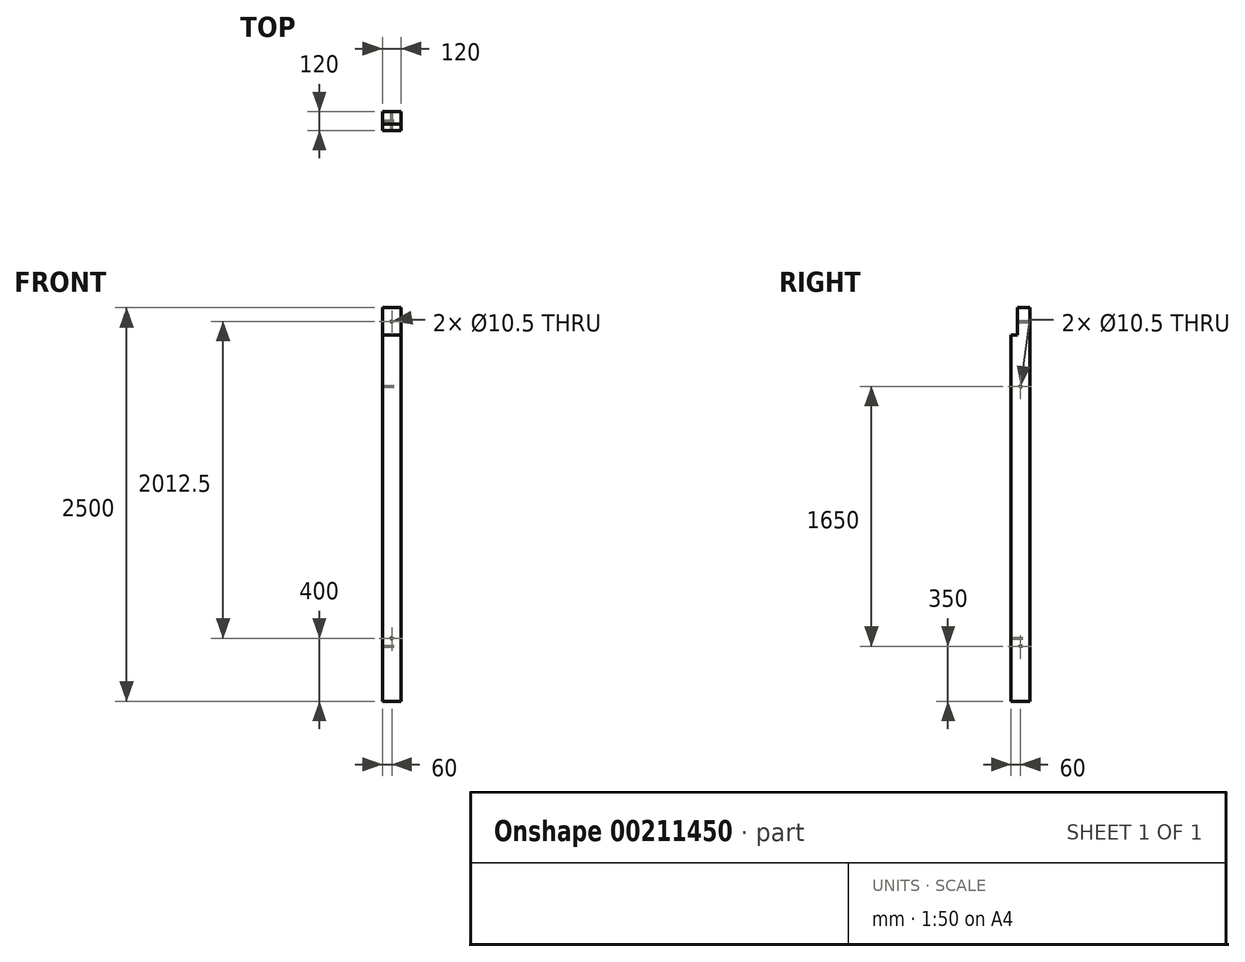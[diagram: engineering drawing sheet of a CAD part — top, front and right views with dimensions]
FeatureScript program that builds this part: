
annotation { "Feature Type Name" : "Feature", "Feature Type Description" : "" }
export const myFeature = defineFeature(function(context is Context, id is Id, definition is map)
    precondition{}
    {
        {
            var Q0;
            Q0=qCreatedBy(makeId("Top.planeOp"),FACE);
            var sketch = newSketch(context, id + "F0", { "sketchPlane" : qUnion([Q0])});
            skLineSegment(sketch, "E0", {"start": v(0, 0) * mm, "end": v(0, 330.83) * mm, "construction": true});
            skLineSegment(sketch, "E1", {"start": v(-296.67, 0) * mm, "end": v(360, 0) * mm, "construction": true});
            skLineSegment(sketch, "E2.bottom", {"start": v(60, 60) * mm, "end": v(-60, 60) * mm});
            skLineSegment(sketch, "E2.top", {"start": v(60, -60) * mm, "end": v(-60, -60) * mm});
            skLineSegment(sketch, "E2.left", {"start": v(60, 60) * mm, "end": v(60, -60) * mm});
            skLineSegment(sketch, "E2.right", {"start": v(-60, 60) * mm, "end": v(-60, -60) * mm});
            skPoint(sketch, "E2.middle", {"position": v(0, 0) * mm});
            skPoint(sketch, "E3.visualSharp", {"position": v(-60, 60) * mm});
            skPoint(sketch, "E4.visualSharp", {"position": v(60, 60) * mm});
            skPoint(sketch, "E5.visualSharp", {"position": v(-60, -60) * mm});
            skPoint(sketch, "E6.visualSharp", {"position": v(60, -60) * mm});
            skSolve(sketch);
        }
        {
            var Q0;
            Q0=qSketchRegion(id+"F0",true);
            extrude(context, id + "F1", {"entities" : qUnion([Q0]), "depth" : 2500 * mm, "symmetric" : true});
        }
        {
            var Q0;
            Q0=makeQuery(id+"F1.opExtrude","SWEPT_FACE",FACE,{"disambiguationData":[OSD([sQuery(id+"F0.wireOp",EDGE,"E2.left")])]});
            var sketch = newSketch(context, id + "F2", { "sketchPlane" : qUnion([Q0])});
            skLineSegment(sketch, "E7.bottom", {"start": v(-60, 1250) * mm, "end": v(-20, 1250) * mm});
            skLineSegment(sketch, "E7.top", {"start": v(-60, 1075) * mm, "end": v(-20, 1075) * mm});
            skLineSegment(sketch, "E7.left", {"start": v(-60, 1250) * mm, "end": v(-60, 1075) * mm});
            skLineSegment(sketch, "E7.right", {"start": v(-20, 1250) * mm, "end": v(-20, 1075) * mm});
            skSolve(sketch);
        }
        {
            var Q0;
            Q0=qSketchRegion(id+"F2",true);
            extrude(context, id + "F3", {"entities" : qUnion([Q0]), "operationType" : NewBodyOperationType.REMOVE, "endBound" : BoundingType.UP_TO_NEXT, "oppositeDirection" : true, "depth" : 25 * mm});
        }
        {
            var Q0;
            Q0=makeQuery(id+"F1.opExtrude","SWEPT_FACE",FACE,{"disambiguationData":[OSD([sQuery(id+"F0.wireOp",EDGE,"E2.bottom")])]});
            var sketch = newSketch(context, id + "F4", { "sketchPlane" : qUnion([Q0])});
            skCircle(sketch, "E8", {"center": v(0, 1162.5) * mm, "radius": 5.25 * mm});
            skCircle(sketch, "E9", {"center": v(0, -850) * mm, "radius": 5.25 * mm});
            skSolve(sketch);
        }
        {
            var Q0;
            Q0=qSketchRegion(id+"F4",true);
            extrude(context, id + "F5", {"entities" : qUnion([Q0]), "operationType" : NewBodyOperationType.REMOVE, "endBound" : BoundingType.THROUGH_ALL, "oppositeDirection" : true, "depth" : 25 * mm});
        }
        {
            var Q0;
            Q0=makeQuery(id+"F1.opExtrude","SWEPT_FACE",FACE,{"disambiguationData":[OSD([sQuery(id+"F0.wireOp",EDGE,"E2.left")])]});
            var sketch = newSketch(context, id + "F6", { "sketchPlane" : qUnion([Q0])});
            skCircle(sketch, "E10", {"center": v(0, -900) * mm, "radius": 5.25 * mm});
            skCircle(sketch, "E11", {"center": v(0, 750) * mm, "radius": 5.25 * mm});
            skSolve(sketch);
        }
        {
            var Q0;
            Q0=qSketchRegion(id+"F6",true);
            extrude(context, id + "F7", {"entities" : qUnion([Q0]), "operationType" : NewBodyOperationType.REMOVE, "endBound" : BoundingType.THROUGH_ALL, "oppositeDirection" : true, "depth" : 25 * mm});
        }
    });
